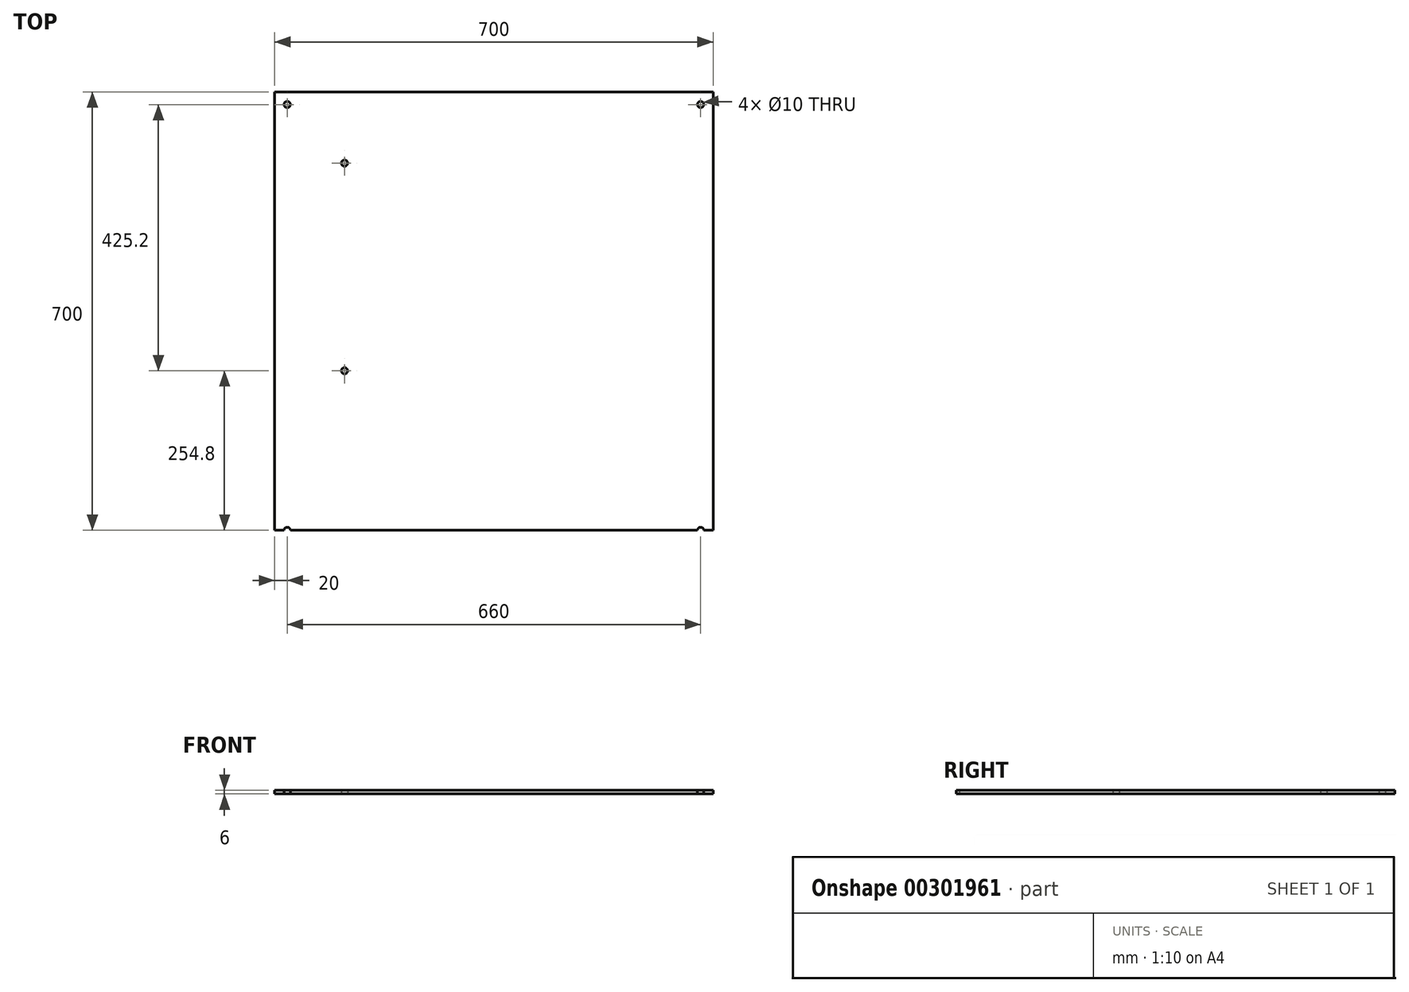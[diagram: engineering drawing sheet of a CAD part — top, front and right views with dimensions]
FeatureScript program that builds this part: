
annotation { "Feature Type Name" : "Feature", "Feature Type Description" : "" }
export const myFeature = defineFeature(function(context is Context, id is Id, definition is map)
    precondition{}
    {
        {
            var Q0;
            Q0=qCreatedBy(makeId("Top.planeOp"),FACE);
            var sketch = newSketch(context, id + "F0", { "sketchPlane" : qUnion([Q0])});
            skLineSegment(sketch, "E0.bottom", {"start": v(350, 350) * mm, "end": v(-350, 350) * mm});
            skLineSegment(sketch, "E0.top", {"start": v(350, -350) * mm, "end": v(-350, -350) * mm});
            skLineSegment(sketch, "E0.left", {"start": v(350, 350) * mm, "end": v(350, -350) * mm});
            skLineSegment(sketch, "E0.right", {"start": v(-350, 350) * mm, "end": v(-350, -350) * mm});
            skPoint(sketch, "E0.middle", {"position": v(0, 0) * mm});
            skPoint(sketch, "E1", {"position": v(-330, 330) * mm});
            skPoint(sketch, "E2", {"position": v(330, 330) * mm});
            skPoint(sketch, "E3", {"position": v(330, -350) * mm});
            skPoint(sketch, "E4", {"position": v(-330, -350) * mm});
            skPoint(sketch, "E5", {"position": v(-238.5, 236.4) * mm});
            skPoint(sketch, "E6", {"position": v(-238.5, -95.2) * mm});
            skSolve(sketch);
        }
        {
            var Q0;
            Q0=makeQuery(id+"F0.imprint","IMPRINT",FACE,{"disambiguationData":[TD([[makeQuery(id+"F0.imprint","IMPRINT",EDGE,{"derivedFrom":sQuery(id+"F0.wireOp",EDGE,"E0.bottom")}),1.0]])]});
            extrude(context, id + "F1", {"entities" : qUnion([Q0]), "depth" : 6 * mm, "offsetDistance" : 25 * mm});
        }
        {
            var Q0;
            Q0=sQuery(id+"F0.wireOp",VERTEX,"E1");
            var Q1;
            Q1=sQuery(id+"F0.wireOp",VERTEX,"E2");
            var Q2;
            Q2=sQuery(id+"F0.wireOp",VERTEX,"E3");
            var Q3;
            Q3=sQuery(id+"F0.wireOp",VERTEX,"E4");
            var Q4;
            Q4=sQuery(id+"F0.wireOp",VERTEX,"E5");
            var Q5;
            Q5=sQuery(id+"F0.wireOp",VERTEX,"E6");
            var Q6;
            Q6=makeQuery(id+"F1.opExtrude","SWEPT_BODY",BODY,{"disambiguationData":[OSD([sQuery(id+"F0.wireOp",EDGE,"E0.bottom"),sQuery(id+"F0.wireOp",EDGE,"E0.top"),sQuery(id+"F0.wireOp",EDGE,"E0.left"),sQuery(id+"F0.wireOp",EDGE,"E0.right")])]});
            hole(context, id + "F2", {"style" : HoleStyle.SIMPLE, "endStyle" : HoleEndStyle.BLIND, "oppositeDirection" : true, "holeDiameter" : 10 * mm, "holeDepth" : 12 * mm, "tappedDepth" : 12 * mm, "tapClearance" : 3, "locations" : qUnion([Q0, Q1, Q2, Q3, Q4, Q5]), "scope" : qUnion([Q6]), "majorDiameter" : 5 * mm});
        }
    });
